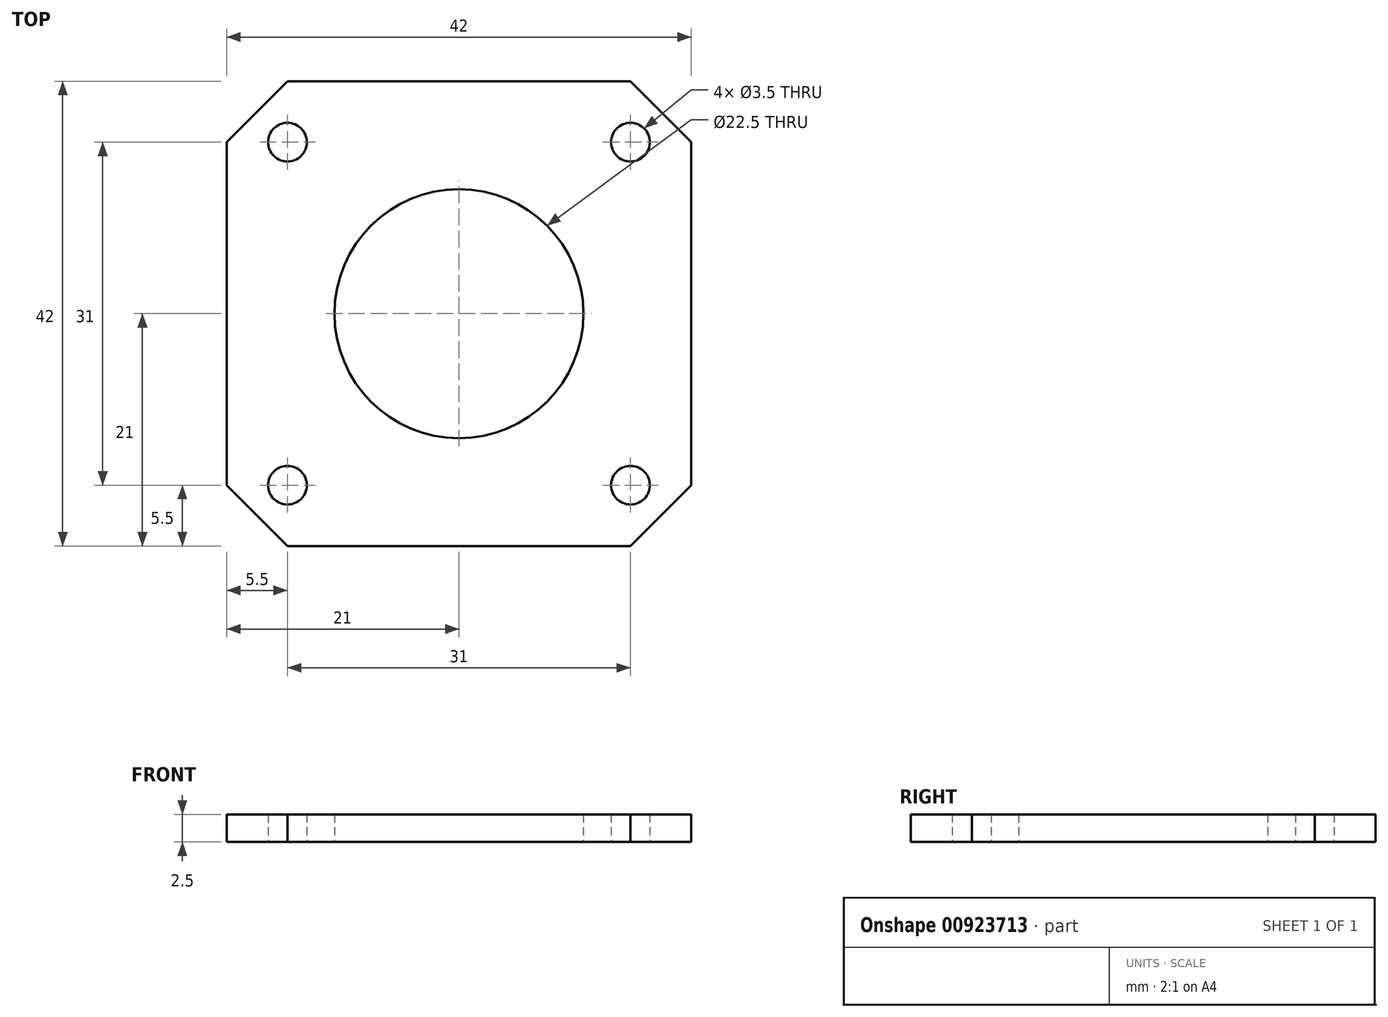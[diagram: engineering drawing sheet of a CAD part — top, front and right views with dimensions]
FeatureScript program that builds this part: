
annotation { "Feature Type Name" : "Feature", "Feature Type Description" : "" }
export const myFeature = defineFeature(function(context is Context, id is Id, definition is map)
    precondition{}
    {
        {
            var Q0;
            Q0=qCreatedBy(makeId("Top.planeOp"),FACE);
            var sketch = newSketch(context, id + "F0", { "sketchPlane" : qUnion([Q0])});
            skLineSegment(sketch, "E0.bottom", {"start": v(21, -21) * mm, "end": v(-21, -21) * mm});
            skLineSegment(sketch, "E0.top", {"start": v(21, 21) * mm, "end": v(-21, 21) * mm});
            skLineSegment(sketch, "E0.left", {"start": v(21, -21) * mm, "end": v(21, 21) * mm});
            skLineSegment(sketch, "E0.right", {"start": v(-21, -21) * mm, "end": v(-21, 21) * mm});
            skPoint(sketch, "E0.middle", {"position": v(0, 0) * mm});
            skLineSegment(sketch, "E1.bottom", {"start": v(15.5, -15.5) * mm, "end": v(-15.5, -15.5) * mm, "construction": true});
            skLineSegment(sketch, "E1.top", {"start": v(15.5, 15.5) * mm, "end": v(-15.5, 15.5) * mm, "construction": true});
            skLineSegment(sketch, "E1.left", {"start": v(15.5, -15.5) * mm, "end": v(15.5, 15.5) * mm, "construction": true});
            skLineSegment(sketch, "E1.right", {"start": v(-15.5, -15.5) * mm, "end": v(-15.5, 15.5) * mm, "construction": true});
            skCircle(sketch, "E2", {"center": v(0, 0) * mm, "radius": 11.25 * mm});
            skCircle(sketch, "E3", {"center": v(-15.5, 15.5) * mm, "radius": 1.75 * mm});
            skCircle(sketch, "E4", {"center": v(15.5, 15.5) * mm, "radius": 1.75 * mm});
            skCircle(sketch, "E5", {"center": v(-15.5, -15.5) * mm, "radius": 1.75 * mm});
            skCircle(sketch, "E6", {"center": v(15.5, -15.5) * mm, "radius": 1.75 * mm});
            skLineSegment(sketch, "E7", {"start": v(21, 15.5) * mm, "end": v(15.5, 21) * mm});
            skLineSegment(sketch, "E8", {"start": v(-21, 15.5) * mm, "end": v(-15.5, 21) * mm});
            skLineSegment(sketch, "E9", {"start": v(-15.5, -21) * mm, "end": v(-21, -15.5) * mm});
            skLineSegment(sketch, "E10", {"start": v(15.5, -21) * mm, "end": v(21, -15.5) * mm});
            skSolve(sketch);
        }
        {
            var Q0;
            Q0=makeQuery(id+"F0.imprint","IMPRINT",FACE,{"disambiguationData":[TD([[makeQuery(id+"F0.imprint","IMPRINT",EDGE,{"derivedFrom":sQuery(id+"F0.wireOp",EDGE,"E2")}),-1.0]])]});
            extrude(context, id + "F1", {"entities" : qUnion([Q0]), "depth" : 2.5 * mm, "offsetDistance" : 25 * mm});
        }
    });
